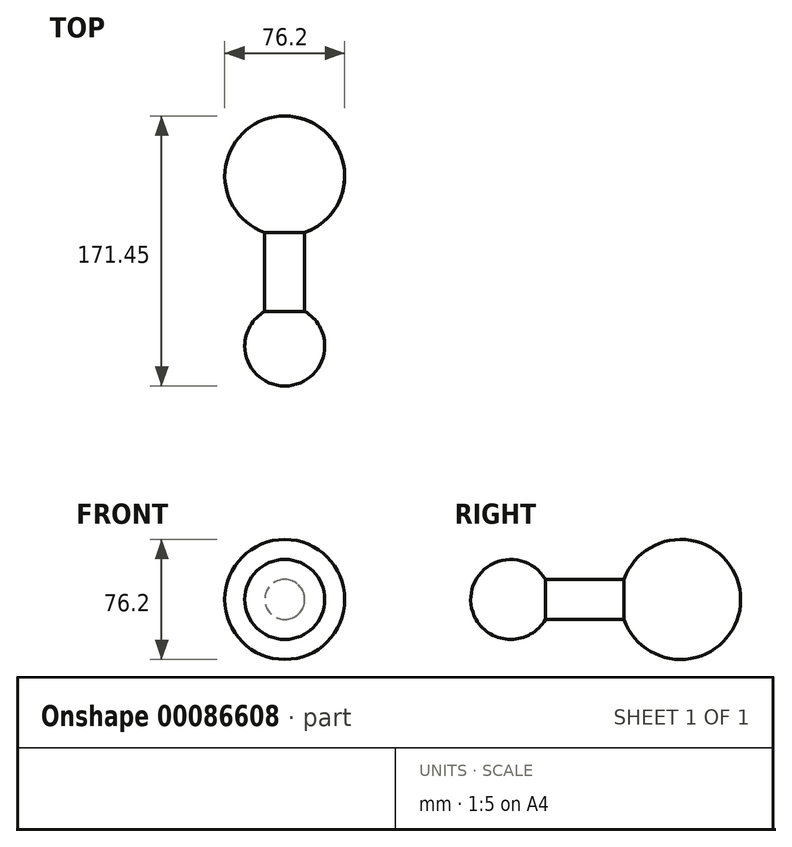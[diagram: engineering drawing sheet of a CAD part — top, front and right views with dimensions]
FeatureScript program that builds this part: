
annotation { "Feature Type Name" : "Feature", "Feature Type Description" : "" }
export const myFeature = defineFeature(function(context is Context, id is Id, definition is map)
    precondition{}
    {
        {
            var Q0;
            Q0=qCreatedBy(makeId("Top.planeOp"),FACE);
            var sketch = newSketch(context, id + "F0", { "sketchPlane" : qUnion([Q0])});
            skArc(sketch, "E0", {"start": v(0, -38.1) * mm, "mid": v(38.1, 0) * mm, "end": v(0, 38.1) * mm});
            skLineSegment(sketch, "E1", {"start": v(0, 0) * mm, "end": v(0, -38.1) * mm});
            skLineSegment(sketch, "E2", {"start": v(0, -38.1) * mm, "end": v(0, 38.1) * mm});
            skSolve(sketch);
        }
        {
            var Q0;
            {var subQ0=sQuery(id+"F0.wireOp",EDGE,"E0");Q0=makeQuery(id+"F0.imprint","IMPRINT",FACE,{"disambiguationData":[TD([[makeQuery(id+"F0.imprint","IMPRINT",EDGE,{"derivedFrom":subQ0}),1.0]])]});}
            var Q1;
            Q1=sQuery(id+"F0.wireOp",EDGE,"E2");
            revolve(context, id + "F1", {"entities" : qUnion([Q0]), "axis" : qUnion([Q1]), "revolveType" : RevolveType.FULL});
        }
        {
            var Q0;
            Q0=qCreatedBy(makeId("Front.planeOp"),FACE);
            var sketch = newSketch(context, id + "F2", { "sketchPlane" : qUnion([Q0])});
            skCircle(sketch, "E3", {"center": v(0, 0) * mm, "radius": 12.7 * mm});
            skSolve(sketch);
        }
        {
            var Q0;
            Q0 = qSketchRegion(id + "F2", true);
            extrude(context, id + "F3", {"entities" : qUnion([Q0]), "operationType" : NewBodyOperationType.ADD, "depth" : 101.6 * mm});
        }
        {
            var Q0;
            Q0=makeQuery(id+"F3.opExtrude","CAP_FACE",FACE,{"disambiguationData":[OSD([sQuery(id+"F2.wireOp",EDGE,"E3")])],"isStart":false});
            cPlane(context, id + "F4", {"entities" : qUnion([Q0]), "cplaneType" : CPlaneType.OFFSET, "offset" : 6.35 * mm, "width" : 152.4 * mm, "height" : 152.4 * mm});
        }
        {
            var Q0;
            Q0=qCreatedBy(id+"F4.planeOp",FACE);
            var sketch = newSketch(context, id + "F5", { "sketchPlane" : qUnion([Q0])});
            skArc(sketch, "E4", {"start": v(-25.4, 0) * mm, "mid": v(0, -25.4) * mm, "end": v(25.4, 0) * mm});
            skLineSegment(sketch, "E5", {"start": v(0, 0) * mm, "end": v(-25.4, 0) * mm});
            skLineSegment(sketch, "E6", {"start": v(-25.4, 0) * mm, "end": v(25.4, 0) * mm});
            skSolve(sketch);
        }
        {
            var Q0;
            {var subQ0=sQuery(id+"F5.wireOp",EDGE,"E4");Q0=makeQuery(id+"F5.imprint","IMPRINT",FACE,{"disambiguationData":[TD([[makeQuery(id+"F5.imprint","IMPRINT",EDGE,{"derivedFrom":subQ0}),1.0]])]});}
            var Q1;
            Q1=sQuery(id+"F5.wireOp",EDGE,"E6");
            revolve(context, id + "F6", {"operationType" : NewBodyOperationType.ADD, "entities" : qUnion([Q0]), "axis" : qUnion([Q1]), "revolveType" : RevolveType.FULL});
        }
    });
